# Revit family: Shower-Valves_and_Controls-KALLISTA-P29305
name_source: partatom
category: Plumbing Fixtures
units: mm (PartAtom-declared; Revit-internal decimal feet)

## family parameters
Cut with Voids When Loaded = No
Host = Face
Maintain Annotation Orientation = No
OmniClass Number = 23.27.31.00
Part Type = Normal
Room Calculation Point = No
Round Connector Dimension = Use Diameter
Shared = No

## types (2) — shared parameters
ADA Compliant = No
Assembly Code = D2020
CW Connection = Yes
Cold Water Inlet = Cold Water Inlet
Date Modified = 06/26/2025
Default Elevation = 36"
Finish = Kallista-Metal-Brass
Flow Rate = 5 GPM
HW Connection = Yes
Height = 5 7/8"
Hot Water Inlet = Hot Water Inlet
Length = 6 9/16"
Manufacturer = Kallista  Co.
Master Format 2014 = 23 09 13.33
Master Format 2014 Name = Control Valves
Material = Premium Metal Construction
Pressure = 45.00 psi
Product Documentation Link = https://techcomm.kohler.com
Product Name = Rough In
Product Page URL = https://www.kallista.com
Tempered Water Outlet 1 = Tempered Water Outlet 1
Tempered Water Outlet 2 = Tempered Water Outlet 2
URL = https://www.kallista.com
Vent Connection = No
Waste Connection = No
Waste Water Outlet = Waste Water Outlet
WaterSense Certified = No

## per-type parameters (varying)
| type | 00 | Description | Model | Type | WS |
| NA-Stainless Steel | Yes | Pressure Balance Rough-In Assembly with Diverter | P29305-00-NA | 1 | No |
| WS, NA-Stainless Steel | No | Pressure Balance Rough-In Assembly with Stops and Diverter | P29305-WS-NA | 2 | Yes |

## geometry (parser evidence)
native form markers: Sweep x6
no freeform markers — native parametric forms only
